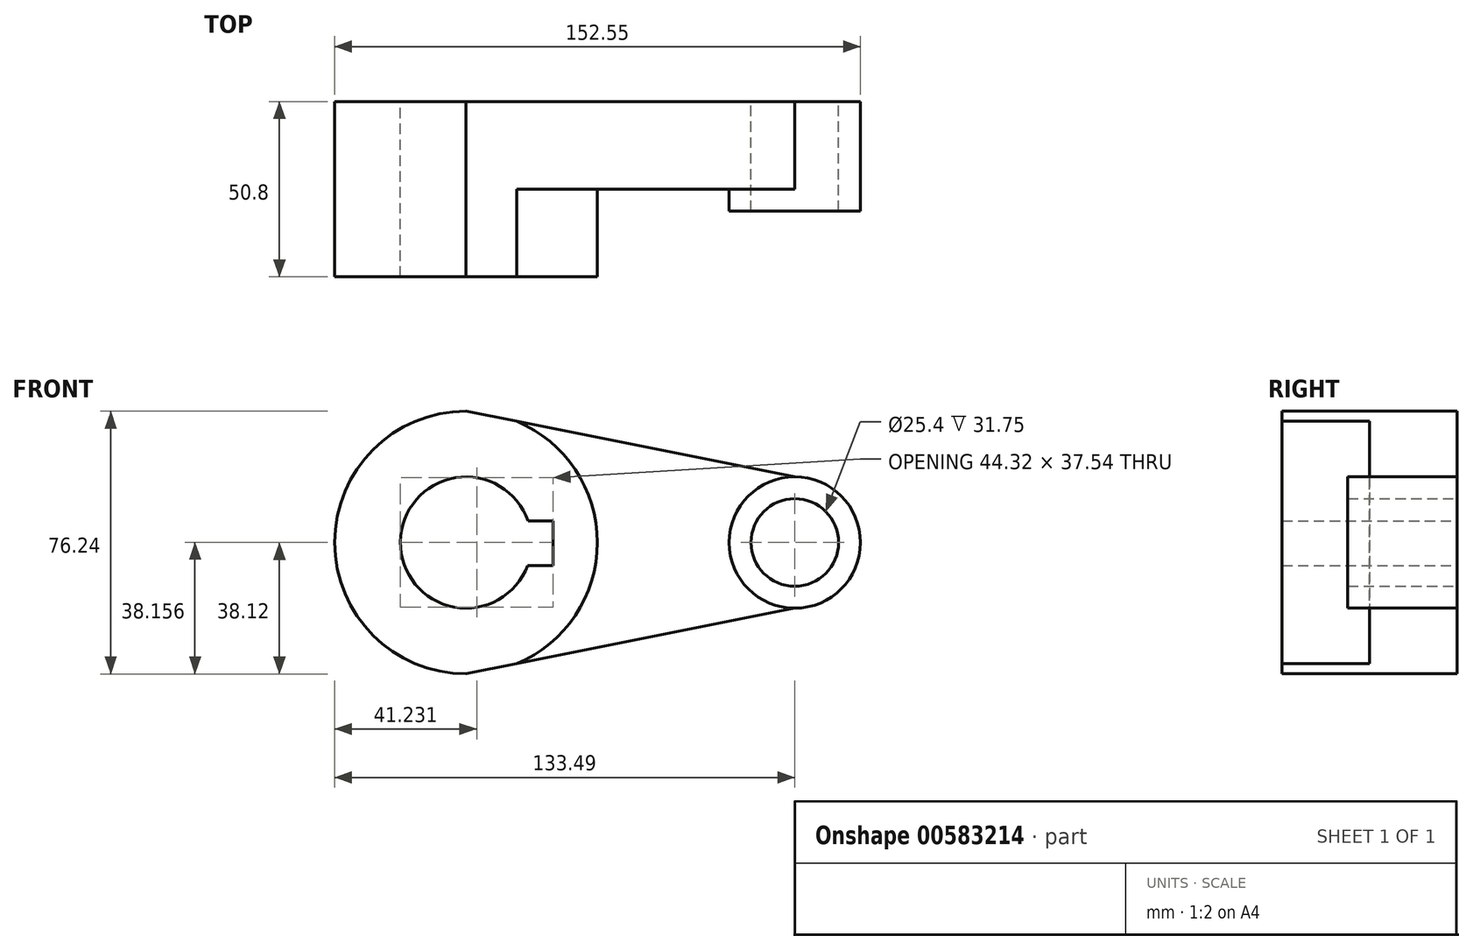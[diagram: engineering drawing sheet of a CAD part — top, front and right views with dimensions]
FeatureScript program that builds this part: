
annotation { "Feature Type Name" : "Feature", "Feature Type Description" : "" }
export const myFeature = defineFeature(function(context is Context, id is Id, definition is map)
    precondition{}
    {
        {
            var Q0;
            Q0=qCreatedBy(makeId("Front.planeOp"),FACE);
            var sketch = newSketch(context, id + "F0", { "sketchPlane" : qUnion([Q0])});
            skCircle(sketch, "E0", {"center": v(-38.12, 0) * mm, "radius": 38.12 * mm});
            skCircle(sketch, "E1", {"center": v(57.25, 0) * mm, "radius": 19.06 * mm});
            skLineSegment(sketch, "E2", {"start": v(57.25, 19.06) * mm, "end": v(-38.12, 38.12) * mm});
            skLineSegment(sketch, "E3", {"start": v(57.25, -19.06) * mm, "end": v(-38.12, -38.12) * mm});
            skCircle(sketch, "E4", {"center": v(-38.12, 0) * mm, "radius": 19.05 * mm});
            skCircle(sketch, "E5", {"center": v(57.25, 0) * mm, "radius": 12.7 * mm});
            skLineSegment(sketch, "E6", {"start": v(-55.98, -6.63) * mm, "end": v(-12.85, -6.63) * mm});
            skLineSegment(sketch, "E7", {"start": v(-12.85, -6.63) * mm, "end": v(-12.85, 6.22) * mm});
            skLineSegment(sketch, "E8", {"start": v(-12.85, 6.22) * mm, "end": v(-56.12, 6.22) * mm});
            skPoint(sketch, "E9.start.orphan", {"position": v(-63.65, 6.22) * mm});
            skPoint(sketch, "E10.start.orphan", {"position": v(-63.65, 0) * mm});
            skSolve(sketch);
        }
        {
            var Q0;
            {var subQ8=sQuery(id+"F0.wireOp",EDGE,"E7");Q0=makeQuery(id+"F0.imprint","IMPRINT",FACE,{"disambiguationData":[TD([[makeQuery(id+"F0.imprint","IMPRINT",EDGE,{"derivedFrom":subQ8}),-1.0]])]});}
            extrude(context, id + "F1", {"entities" : qUnion([Q0]), "depth" : 50.8 * mm, "offsetDistance" : 25.4 * mm});
        }
        {
            var Q0;
            {var subQ0=sQuery(id+"F0.wireOp",EDGE,"E2");var subQ1=sQuery(id+"F0.wireOp",EDGE,"E0");var subQ2=makeQuery(id+"F0.imprint","INTERSECT",VERTEX,{"disambiguationData":[OD(1.0)],"derivedFrom":[subQ1,subQ0]});Q0=makeQuery(id+"F0.imprint","IMPRINT",FACE,{"disambiguationData":[TD([[makeQuery(id+"F0.imprint","IMPRINT",EDGE,{"disambiguationData":[TD([[subQ2,1.0]])],"derivedFrom":subQ1}),-1.0]])]});}
            extrude(context, id + "F2", {"entities" : qUnion([Q0]), "operationType" : NewBodyOperationType.ADD, "depth" : 25.4 * mm, "offsetDistance" : 25.4 * mm});
        }
        {
            var Q0;
            Q0=makeQuery(id+"F0.imprint","IMPRINT",FACE,{"disambiguationData":[TD([[makeQuery(id+"F0.imprint","IMPRINT",EDGE,{"derivedFrom":sQuery(id+"F0.wireOp",EDGE,"E5")}),-1.0]])]});
            extrude(context, id + "F3", {"entities" : qUnion([Q0]), "operationType" : NewBodyOperationType.ADD, "depth" : 31.75 * mm, "offsetDistance" : 25.4 * mm});
        }
    });
